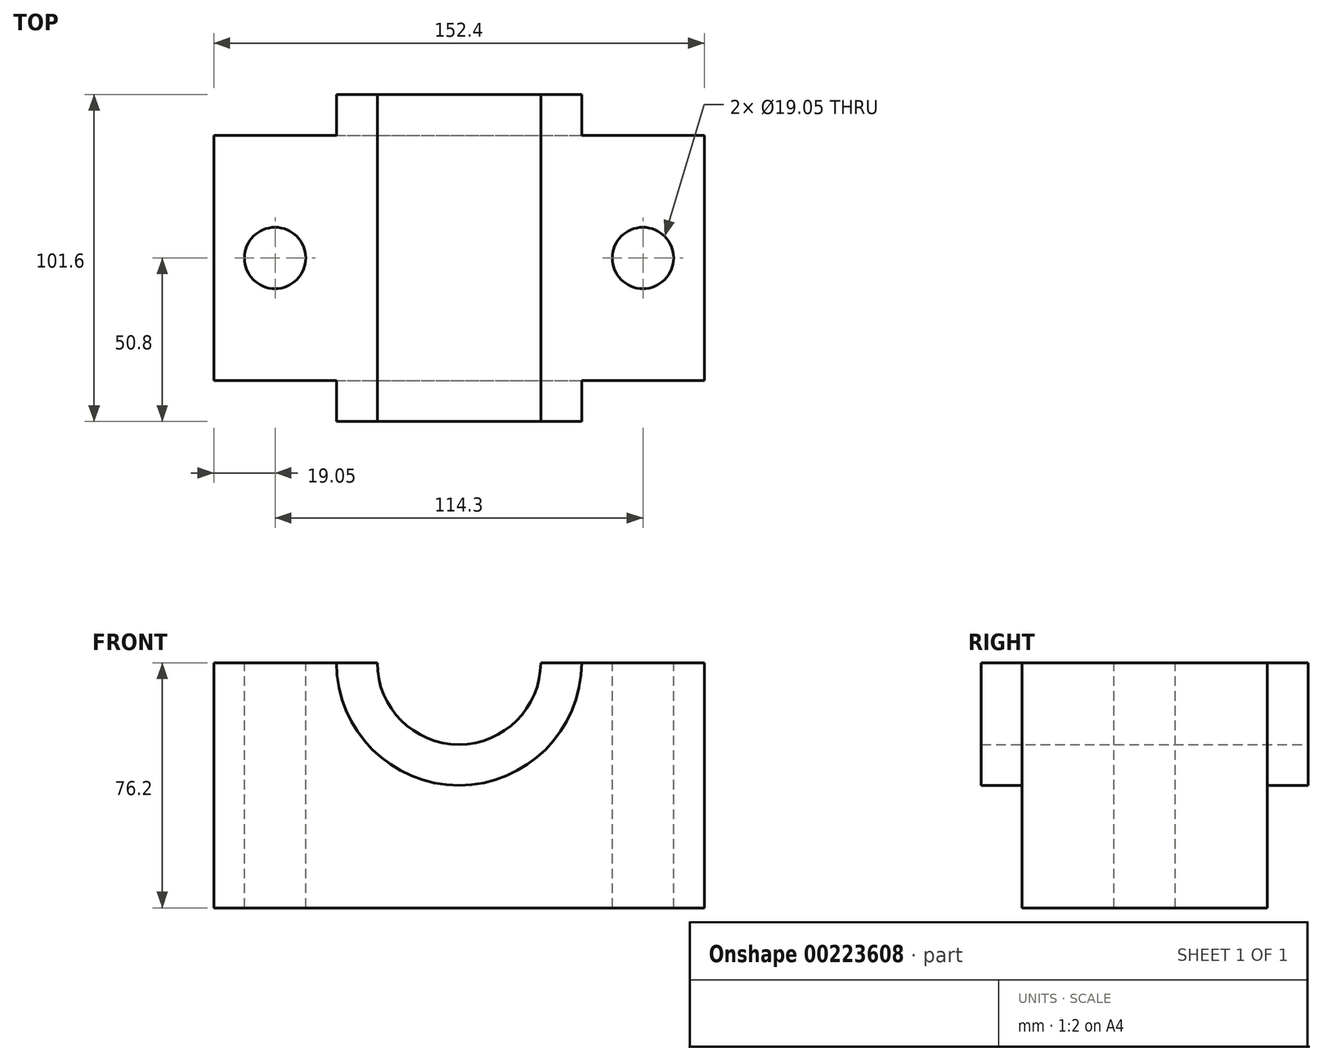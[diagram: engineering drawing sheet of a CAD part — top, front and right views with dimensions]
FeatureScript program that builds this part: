
annotation { "Feature Type Name" : "Feature", "Feature Type Description" : "" }
export const myFeature = defineFeature(function(context is Context, id is Id, definition is map)
    precondition{}
    {
        {
            var Q0;
            Q0=qCreatedBy(makeId("Front.planeOp"),FACE);
            var sketch = newSketch(context, id + "F0", { "sketchPlane" : qUnion([Q0])});
            skLineSegment(sketch, "E0.bottom", {"start": v(-76.2, -38.1) * mm, "end": v(76.2, -38.1) * mm});
            skLineSegment(sketch, "E0.left", {"start": v(-76.2, -38.1) * mm, "end": v(-76.2, 38.1) * mm});
            skLineSegment(sketch, "E0.right", {"start": v(76.2, -38.1) * mm, "end": v(76.2, 38.1) * mm});
            skPoint(sketch, "E0.middle", {"position": v(0, 0) * mm});
            skLineSegment(sketch, "E1", {"start": v(-76.2, 38.1) * mm, "end": v(-38.1, 38.1) * mm});
            skLineSegment(sketch, "E2", {"start": v(76.2, 38.1) * mm, "end": v(38.1, 38.1) * mm});
            skArc(sketch, "E3", {"start": v(-38.1, 38.1) * mm, "mid": v(0, 0) * mm, "end": v(38.1, 38.1) * mm});
            skSolve(sketch);
        }
        {
            var Q0;
            Q0=makeQuery(id+"F0.imprint","IMPRINT",FACE,{"disambiguationData":[TD([[makeQuery(id+"F0.imprint","IMPRINT",EDGE,{"derivedFrom":sQuery(id+"F0.wireOp",EDGE,"E0.bottom")}),1.0]])]});
            extrude(context, id + "F1", {"entities" : qUnion([Q0]), "endBound" : BoundingType.SYMMETRIC, "depth" : 76.2 * mm});
        }
        {
            var Q0;
            Q0=makeQuery(id+"F1.opExtrude","CAP_FACE",FACE,{"disambiguationData":[OSD([sQuery(id+"F0.wireOp",EDGE,"E0.bottom"),sQuery(id+"F0.wireOp",EDGE,"E0.left"),sQuery(id+"F0.wireOp",EDGE,"E0.right"),sQuery(id+"F0.wireOp",EDGE,"E1"),sQuery(id+"F0.wireOp",EDGE,"E2"),sQuery(id+"F0.wireOp",EDGE,"E3")])],"isStart":false});
            var sketch = newSketch(context, id + "F2", { "sketchPlane" : qUnion([Q0])});
            skLineSegment(sketch, "E4", {"start": v(-38.1, 38.1) * mm, "end": v(-25.4, 38.1) * mm});
            skLineSegment(sketch, "E5", {"start": v(38.1, 38.1) * mm, "end": v(25.4, 38.1) * mm});
            skArc(sketch, "E6", {"start": v(-25.4, 38.1) * mm, "mid": v(0, 12.7) * mm, "end": v(25.4, 38.1) * mm});
            skSolve(sketch);
        }
        {
            var Q0;
            Q0=makeQuery(id+"F2.imprint","IMPRINT",FACE,{"disambiguationData":[TD([[makeQuery(id+"F2.imprint","IMPRINT",EDGE,{"derivedFrom":sQuery(id+"F2.wireOp",EDGE,"E4")}),-1.0]])]});
            extrude(context, id + "F3", {"entities" : qUnion([Q0]), "operationType" : NewBodyOperationType.ADD, "depth" : 12.7 * mm, "hasSecondDirection" : true, "secondDirectionOppositeDirection" : true, "secondDirectionDepth" : 88.9 * mm});
        }
        {
            var Q0;
            Q0=makeQuery(id+"F3.boolean.opBoolean","MERGE",FACE,{"derivedFrom":[makeQuery(id+"F1.opExtrude","SWEPT_FACE",FACE,{"disambiguationData":[OSD([sQuery(id+"F0.wireOp",EDGE,"E1")])]}),makeQuery(id+"F3.opExtrude","SWEPT_FACE",FACE,{"disambiguationData":[OSD([sQuery(id+"F2.wireOp",EDGE,"E4")])]})]});
            var sketch = newSketch(context, id + "F4", { "sketchPlane" : qUnion([Q0])});
            skCircle(sketch, "E7", {"center": v(-57.15, 0) * mm, "radius": 9.53 * mm});
            skSolve(sketch);
        }
        {
            var Q0;
            Q0=makeQuery(id+"F3.boolean.opBoolean","MERGE",FACE,{"derivedFrom":[makeQuery(id+"F1.opExtrude","SWEPT_FACE",FACE,{"disambiguationData":[OSD([sQuery(id+"F0.wireOp",EDGE,"E2")])]}),makeQuery(id+"F3.opExtrude","SWEPT_FACE",FACE,{"disambiguationData":[OSD([sQuery(id+"F2.wireOp",EDGE,"E5")])]})]});
            var sketch = newSketch(context, id + "F5", { "sketchPlane" : qUnion([Q0])});
            skCircle(sketch, "E8", {"center": v(57.15, 0) * mm, "radius": 9.53 * mm});
            skSolve(sketch);
        }
        {
            var Q0;
            Q0=makeQuery(id+"F4.imprint","IMPRINT",FACE,{"disambiguationData":[TD([[makeQuery(id+"F4.imprint","IMPRINT",EDGE,{"derivedFrom":sQuery(id+"F4.wireOp",EDGE,"E7")}),1.0]])]});
            var Q1;
            Q1=makeQuery(id+"F5.imprint","IMPRINT",FACE,{"disambiguationData":[TD([[makeQuery(id+"F5.imprint","IMPRINT",EDGE,{"derivedFrom":sQuery(id+"F5.wireOp",EDGE,"E8")}),1.0]])]});
            extrude(context, id + "F6", {"entities" : qUnion([Q0, Q1]), "operationType" : NewBodyOperationType.REMOVE, "oppositeDirection" : true, "depth" : 113.03 * mm});
        }
    });
